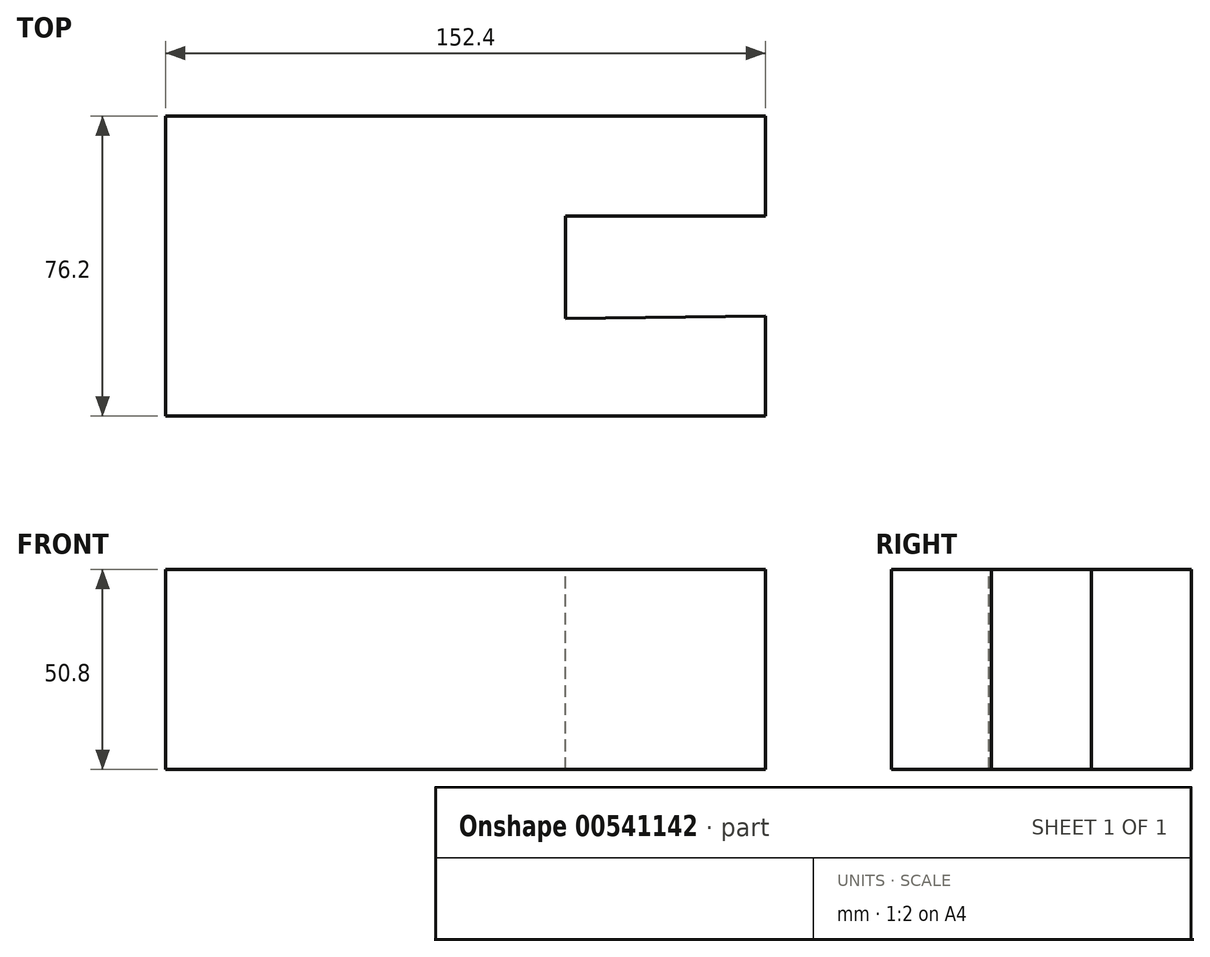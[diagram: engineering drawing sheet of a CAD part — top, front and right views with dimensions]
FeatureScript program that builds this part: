
annotation { "Feature Type Name" : "Feature", "Feature Type Description" : "" }
export const myFeature = defineFeature(function(context is Context, id is Id, definition is map)
    precondition{}
    {
        {
            var Q0;
            Q0=qCreatedBy(makeId("Top.planeOp"),FACE);
            var sketch = newSketch(context, id + "F0", { "sketchPlane" : qUnion([Q0])});
            skLineSegment(sketch, "E0", {"start": v(-73.74, 69.73) * mm, "end": v(78.66, 69.73) * mm});
            skLineSegment(sketch, "E1", {"start": v(78.66, 69.73) * mm, "end": v(78.66, 44.33) * mm});
            skLineSegment(sketch, "E2", {"start": v(78.66, 44.33) * mm, "end": v(27.86, 44.33) * mm});
            skLineSegment(sketch, "E3", {"start": v(27.86, 44.33) * mm, "end": v(27.86, 18.35) * mm});
            skLineSegment(sketch, "E4", {"start": v(27.86, 18.35) * mm, "end": v(78.65, 18.93) * mm});
            skLineSegment(sketch, "E5", {"start": v(78.65, 18.93) * mm, "end": v(78.65, -6.47) * mm});
            skLineSegment(sketch, "E6", {"start": v(78.65, -6.47) * mm, "end": v(-73.74, -6.47) * mm});
            skLineSegment(sketch, "E7", {"start": v(-73.74, -6.47) * mm, "end": v(-73.74, 69.73) * mm});
            skSolve(sketch);
        }
        {
            var Q0;
            Q0 = qSketchRegion(id + "F0", true);
            extrude(context, id + "F1", {"entities" : qUnion([Q0]), "oppositeDirection" : true, "depth" : 50.8 * mm, "offsetDistance" : 25.4 * mm});
        }
    });
